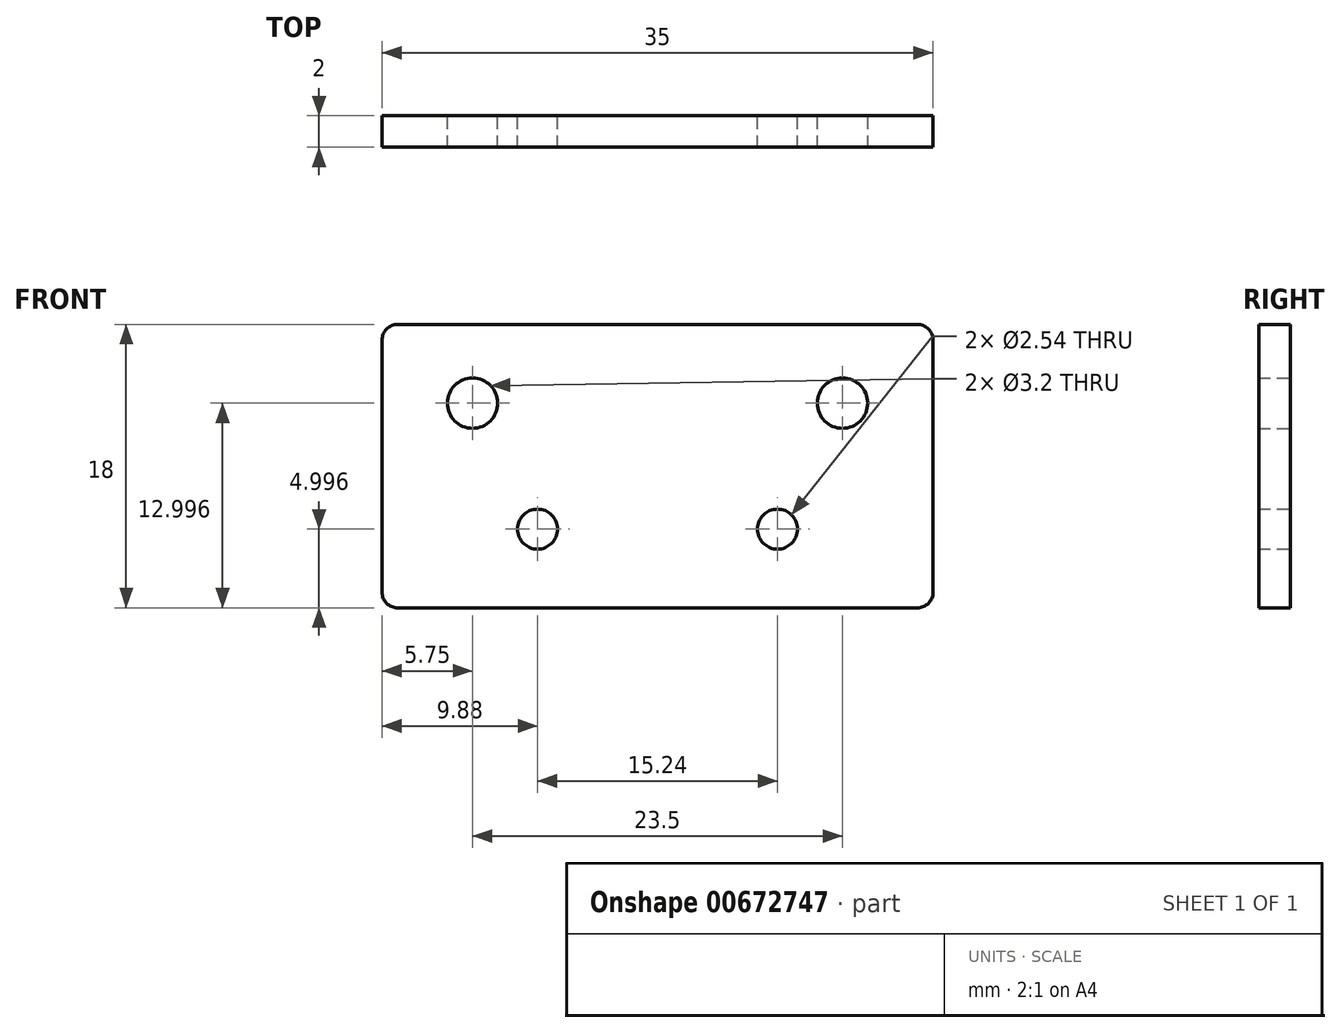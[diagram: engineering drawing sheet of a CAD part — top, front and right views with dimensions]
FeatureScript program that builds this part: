
annotation { "Feature Type Name" : "Feature", "Feature Type Description" : "" }
export const myFeature = defineFeature(function(context is Context, id is Id, definition is map)
    precondition{}
    {
        {
            var Q0;
            Q0=qCreatedBy(makeId("Front.planeOp"),FACE);
            var sketch = newSketch(context, id + "F0", { "sketchPlane" : qUnion([Q0])});
            skLineSegment(sketch, "E0.bottom", {"start": v(-28.25, 17.95) * mm, "end": v(4.75, 17.95) * mm});
            skLineSegment(sketch, "E0.top", {"start": v(-28.25, -0.05) * mm, "end": v(4.75, -0.05) * mm});
            skLineSegment(sketch, "E0.left", {"start": v(-29.25, 16.95) * mm, "end": v(-29.25, 0.95) * mm});
            skLineSegment(sketch, "E0.right", {"start": v(5.75, 16.95) * mm, "end": v(5.75, 0.95) * mm});
            skCircle(sketch, "E1", {"center": v(-19.37, 4.95) * mm, "radius": 1.27 * mm});
            skCircle(sketch, "E2", {"center": v(-4.13, 4.95) * mm, "radius": 1.27 * mm});
            skPoint(sketch, "E3.visualSharp", {"position": v(-29.25, 17.95) * mm});
            skArc(sketch, "E3.filletArc", {"start": v(-28.25, 17.95) * mm, "mid": v(-28.96, 17.65) * mm, "end": v(-29.25, 16.95) * mm});
            skPoint(sketch, "E4.visualSharp", {"position": v(5.75, 17.95) * mm});
            skArc(sketch, "E4.filletArc", {"start": v(5.75, 16.95) * mm, "mid": v(5.46, 17.65) * mm, "end": v(4.75, 17.95) * mm});
            skPoint(sketch, "E5.visualSharp", {"position": v(5.75, -0.05) * mm});
            skArc(sketch, "E5.filletArc", {"start": v(4.75, -0.05) * mm, "mid": v(5.46, 0.24) * mm, "end": v(5.75, 0.95) * mm});
            skPoint(sketch, "E6.visualSharp", {"position": v(-29.25, -0.05) * mm});
            skArc(sketch, "E6.filletArc", {"start": v(-29.25, 0.95) * mm, "mid": v(-28.96, 0.24) * mm, "end": v(-28.25, -0.05) * mm});
            skCircle(sketch, "E7", {"center": v(0, 12.95) * mm, "radius": 1.6 * mm});
            skCircle(sketch, "E8", {"center": v(-23.5, 12.95) * mm, "radius": 1.6 * mm});
            skSolve(sketch);
        }
        {
            var Q0;
            Q0=makeQuery(id+"F0.imprint","IMPRINT",FACE,{"disambiguationData":[TD([[makeQuery(id+"F0.imprint","IMPRINT",EDGE,{"derivedFrom":sQuery(id+"F0.wireOp",EDGE,"E0.bottom")}),-1.0]])]});
            extrude(context, id + "F1", {"entities" : qUnion([Q0]), "depth" : 2 * mm, "offsetDistance" : 25 * mm});
        }
    });
